# Revit family: Salon_CB-561_BIM
name_source: partatom
category: Arredi
units: mm (PartAtom-declared; Revit-internal decimal feet)

## family parameters
Attiva taglio nelle viste = No
Basato su piano di lavoro = No
Condiviso = No
Numero OmniClass = 23.40.20.00
Origine composizione di rendering = Geometria famiglia
Punto di calcolo locali = No
Sempre verticale = Sì
Taglio con vuoti quando caricato = No
Titolo OmniClass = General Furniture and Specialties

## types (2) — shared parameters
BASE MATERIAL = BASSAM_FELLOWS_COMFORT_LEATHER_02067_BEIGE
BIM BADGE = https://bim.archiproducts.com
COLLECTION = Salon
DEPTH = 724 mm  [stored 2.37533 ft]
Descrizione = Club chair with armrests
FEET MATERIAL = BASSAM_FELLOWS_WALNUT_BLACK_OIL_W-BO
HEIGHT = 692 mm
PRODUCT SHEET = https://www.archiproducts.com
Produttore = BassamFellows
SWIVEL MATERIAL = BASSAM_FELLOWS_MATT_BLACK_BP
TECHNICAL SHEET = https://bassamfellows.com
UPHOLSTERY MATERIAL = BASSAM_FELLOWS_COMFORT_LEATHER_02067_BEIGE
URL = https://bassamfellows.com
WIDTH = 685 mm
zero-valued in all types: Prospetto di default

## per-type parameters (varying)
| type | MATERIAL DESCRIPTION | Modello | NO SWIVEL | SWIVEL |
| CB-561S | Multilayered plywood inner frame; seat support with a combination of foam and memory foam; arm and back in foam; seat and bolster cushions in feather and down. Swivel steel base. | Salon Club Chair (Swivel Base) | No | Sì |
| CB-561 | Multilayered plywood inner frame; seat support with a combination of foam and memory foam; arm and back in foam; seat and bolster cushions in feather and down. | Salon Club Chair | Sì | No |

note: column(s) folded — value = type name in every type: PRODUCT CODE

note: [stored X ft] marks values corroborated as IEEE doubles in the binary element streams (Revit-internal decimal feet)

## geometry (parser evidence)
native form markers: Sweep x2
no freeform markers — native parametric forms only
